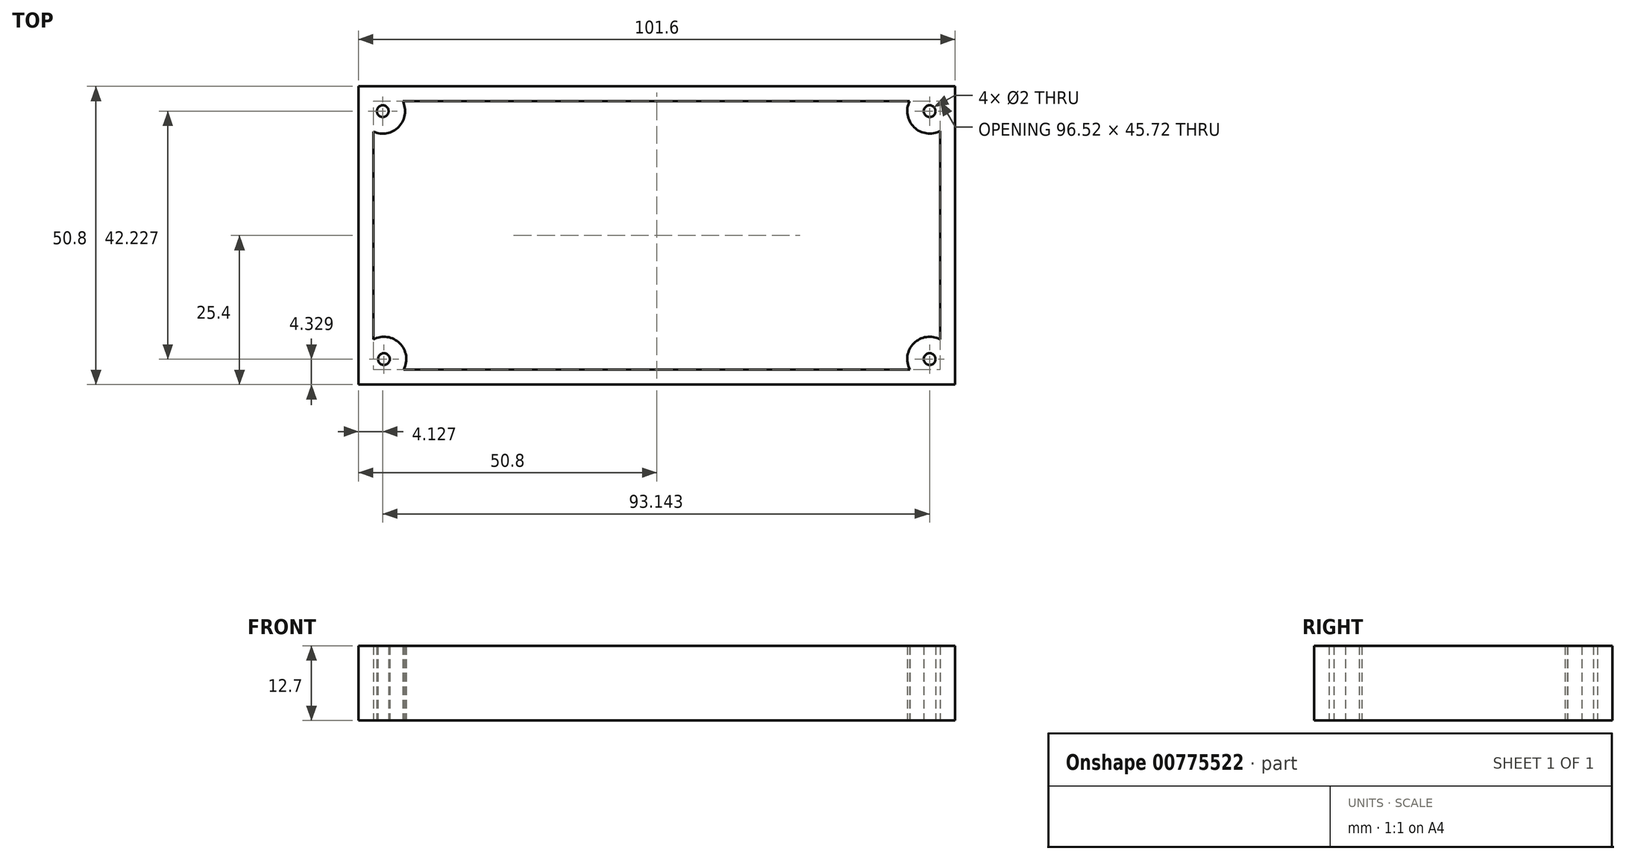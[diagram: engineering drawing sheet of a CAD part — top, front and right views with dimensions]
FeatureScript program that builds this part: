
annotation { "Feature Type Name" : "Feature", "Feature Type Description" : "" }
export const myFeature = defineFeature(function(context is Context, id is Id, definition is map)
    precondition{}
    {
        {
            var Q0;
            Q0=qCreatedBy(makeId("Top.planeOp"),FACE);
            var sketch = newSketch(context, id + "F0", { "sketchPlane" : qUnion([Q0])});
            skLineSegment(sketch, "E0.bottom", {"start": v(-50.8, 24.75) * mm, "end": v(50.8, 24.75) * mm});
            skLineSegment(sketch, "E0.top", {"start": v(-50.8, -26.05) * mm, "end": v(50.8, -26.05) * mm});
            skLineSegment(sketch, "E0.left", {"start": v(-50.8, 24.75) * mm, "end": v(-50.8, -26.05) * mm});
            skLineSegment(sketch, "E0.right", {"start": v(50.8, 24.75) * mm, "end": v(50.8, -26.05) * mm});
            skLineSegment(sketch, "E1.0", {"start": v(-43.26, 22.21) * mm, "end": v(43.06, 22.21) * mm});
            skLineSegment(sketch, "E1.1", {"start": v(-48.26, 17.04) * mm, "end": v(-48.26, -18.36) * mm});
            skLineSegment(sketch, "E1.2", {"start": v(-43.1, -23.5) * mm, "end": v(43.1, -23.5) * mm});
            skLineSegment(sketch, "E1.3", {"start": v(48.26, 17.14) * mm, "end": v(48.26, -18.36) * mm});
            skPoint(sketch, "E2", {"position": v(0, 0) * mm});
            skPoint(sketch, "E3.endSnap0", {"position": v(0, -26.05) * mm});
            skArc(sketch, "E4", {"start": v(-48.26, 17.04) * mm, "mid": v(-43.93, 17.86) * mm, "end": v(-43.26, 22.21) * mm});
            skArc(sketch, "E5", {"start": v(43.06, 22.21) * mm, "mid": v(43.81, 17.78) * mm, "end": v(48.26, 17.14) * mm});
            skArc(sketch, "E6", {"start": v(48.26, -18.36) * mm, "mid": v(43.78, -19.03) * mm, "end": v(43.1, -23.5) * mm});
            skArc(sketch, "E7", {"start": v(-43.1, -23.5) * mm, "mid": v(-43.78, -19.03) * mm, "end": v(-48.26, -18.36) * mm});
            skLineSegment(sketch, "E8", {"start": v(-50.8, 0) * mm, "end": v(50.8, 0) * mm, "construction": true});
            skPoint(sketch, "E8.startSnap0", {"position": v(-50.8, -0.65) * mm});
            skLineSegment(sketch, "E9", {"start": v(0, 24.75) * mm, "end": v(0, -26.05) * mm, "construction": true});
            skSolve(sketch);
        }
        {
            var Q0;
            Q0=makeQuery(id+"F0.imprint","IMPRINT",FACE,{"disambiguationData":[TD([[makeQuery(id+"F0.imprint","IMPRINT",EDGE,{"derivedFrom":sQuery(id+"F0.wireOp",EDGE,"E0.bottom")}),-1.0]])]});
            extrude(context, id + "F1", {"entities" : qUnion([Q0]), "depth" : 12.7 * mm, "offsetDistance" : 25.4 * mm});
        }
        {
            var Q0;
            Q0=sQuery(id+"F0.wireOp",VERTEX,"E5.center");
            var Q1;
            Q1=makeQuery(id+"F1.opExtrude","SWEPT_BODY",BODY,{"disambiguationData":[OSD([sQuery(id+"F0.wireOp",EDGE,"E0.bottom"),sQuery(id+"F0.wireOp",EDGE,"E0.top"),sQuery(id+"F0.wireOp",EDGE,"E0.left"),sQuery(id+"F0.wireOp",EDGE,"E0.right"),sQuery(id+"F0.wireOp",EDGE,"E1.0"),sQuery(id+"F0.wireOp",EDGE,"E1.1"),sQuery(id+"F0.wireOp",EDGE,"E1.2"),sQuery(id+"F0.wireOp",EDGE,"E1.3"),sQuery(id+"F0.wireOp",EDGE,"E4"),sQuery(id+"F0.wireOp",EDGE,"E5"),sQuery(id+"F0.wireOp",EDGE,"E6"),sQuery(id+"F0.wireOp",EDGE,"E7")])]});
            hole(context, id + "F2", {"style" : HoleStyle.SIMPLE, "endStyle" : HoleEndStyle.BLIND, "oppositeDirection" : true, "standardTappedOrClearance" : lookupTablePath({ "standard" : "ISO", "size" : "2", "type" : "Drilled" }), "standardBlindInLast" : lookupTablePath({ "standard" : "ISO", "size" : "2", "type" : "Drilled" }), "holeDiameter" : 2 * mm, "majorDiameter" : 3 * mm, "holeDepth" : 14.2 * mm, "isTappedThrough" : true, "tappedDepth" : 12.7 * mm, "tapClearance" : 3, "startFromSketch" : true, "locations" : qUnion([Q0]), "scope" : qUnion([Q1])});
        }
        {
            var Q0;
            Q0=sQuery(id+"F0.wireOp",VERTEX,"E7.center");
            var Q1;
            Q1=makeQuery(id+"F1.opExtrude","SWEPT_BODY",BODY,{"disambiguationData":[OSD([sQuery(id+"F0.wireOp",EDGE,"E0.bottom"),sQuery(id+"F0.wireOp",EDGE,"E0.top"),sQuery(id+"F0.wireOp",EDGE,"E0.left"),sQuery(id+"F0.wireOp",EDGE,"E0.right"),sQuery(id+"F0.wireOp",EDGE,"E1.0"),sQuery(id+"F0.wireOp",EDGE,"E1.1"),sQuery(id+"F0.wireOp",EDGE,"E1.2"),sQuery(id+"F0.wireOp",EDGE,"E1.3"),sQuery(id+"F0.wireOp",EDGE,"E4"),sQuery(id+"F0.wireOp",EDGE,"E5"),sQuery(id+"F0.wireOp",EDGE,"E6"),sQuery(id+"F0.wireOp",EDGE,"E7")])]});
            hole(context, id + "F3", {"style" : HoleStyle.SIMPLE, "endStyle" : HoleEndStyle.BLIND, "oppositeDirection" : true, "standardTappedOrClearance" : lookupTablePath({ "standard" : "ISO", "size" : "2", "type" : "Drilled" }), "standardBlindInLast" : lookupTablePath({ "standard" : "ISO", "size" : "2", "type" : "Drilled" }), "holeDiameter" : 2 * mm, "majorDiameter" : 6.35 * mm, "holeDepth" : 14.2 * mm, "isTappedThrough" : true, "tappedDepth" : 12.7 * mm, "tapClearance" : 3, "locations" : qUnion([Q0]), "scope" : qUnion([Q1])});
        }
        {
            var Q0;
            Q0=sQuery(id+"F0.wireOp",VERTEX,"E6.center");
            var Q1;
            Q1=makeQuery(id+"F1.opExtrude","SWEPT_BODY",BODY,{"disambiguationData":[OSD([sQuery(id+"F0.wireOp",EDGE,"E0.bottom"),sQuery(id+"F0.wireOp",EDGE,"E0.top"),sQuery(id+"F0.wireOp",EDGE,"E0.left"),sQuery(id+"F0.wireOp",EDGE,"E0.right"),sQuery(id+"F0.wireOp",EDGE,"E1.0"),sQuery(id+"F0.wireOp",EDGE,"E1.1"),sQuery(id+"F0.wireOp",EDGE,"E1.2"),sQuery(id+"F0.wireOp",EDGE,"E1.3"),sQuery(id+"F0.wireOp",EDGE,"E4"),sQuery(id+"F0.wireOp",EDGE,"E5"),sQuery(id+"F0.wireOp",EDGE,"E6"),sQuery(id+"F0.wireOp",EDGE,"E7")])]});
            hole(context, id + "F4", {"style" : HoleStyle.SIMPLE, "endStyle" : HoleEndStyle.BLIND, "oppositeDirection" : true, "standardTappedOrClearance" : lookupTablePath({ "standard" : "ISO", "size" : "2", "type" : "Drilled" }), "standardBlindInLast" : lookupTablePath({ "standard" : "ISO", "size" : "2", "type" : "Drilled" }), "holeDiameter" : 2 * mm, "majorDiameter" : 6.35 * mm, "holeDepth" : 14.2 * mm, "isTappedThrough" : true, "tappedDepth" : 12.7 * mm, "tapClearance" : 3, "startFromSketch" : true, "locations" : qUnion([Q0]), "scope" : qUnion([Q1])});
        }
        {
            var Q0;
            Q0=sQuery(id+"F0.wireOp",VERTEX,"E4.center");
            var Q1;
            Q1=makeQuery(id+"F1.opExtrude","SWEPT_BODY",BODY,{"disambiguationData":[OSD([sQuery(id+"F0.wireOp",EDGE,"E0.bottom"),sQuery(id+"F0.wireOp",EDGE,"E0.top"),sQuery(id+"F0.wireOp",EDGE,"E0.left"),sQuery(id+"F0.wireOp",EDGE,"E0.right"),sQuery(id+"F0.wireOp",EDGE,"E1.0"),sQuery(id+"F0.wireOp",EDGE,"E1.1"),sQuery(id+"F0.wireOp",EDGE,"E1.2"),sQuery(id+"F0.wireOp",EDGE,"E1.3"),sQuery(id+"F0.wireOp",EDGE,"E4"),sQuery(id+"F0.wireOp",EDGE,"E5"),sQuery(id+"F0.wireOp",EDGE,"E6"),sQuery(id+"F0.wireOp",EDGE,"E7")])]});
            hole(context, id + "F5", {"style" : HoleStyle.SIMPLE, "endStyle" : HoleEndStyle.BLIND, "oppositeDirection" : true, "standardTappedOrClearance" : lookupTablePath({ "standard" : "ISO", "size" : "2", "type" : "Drilled" }), "standardBlindInLast" : lookupTablePath({ "standard" : "ISO", "size" : "2", "type" : "Drilled" }), "holeDiameter" : 2 * mm, "majorDiameter" : 3 * mm, "holeDepth" : 14.2 * mm, "isTappedThrough" : true, "tappedDepth" : 12.7 * mm, "tapClearance" : 3, "startFromSketch" : true, "locations" : qUnion([Q0]), "scope" : qUnion([Q1])});
        }
    });
